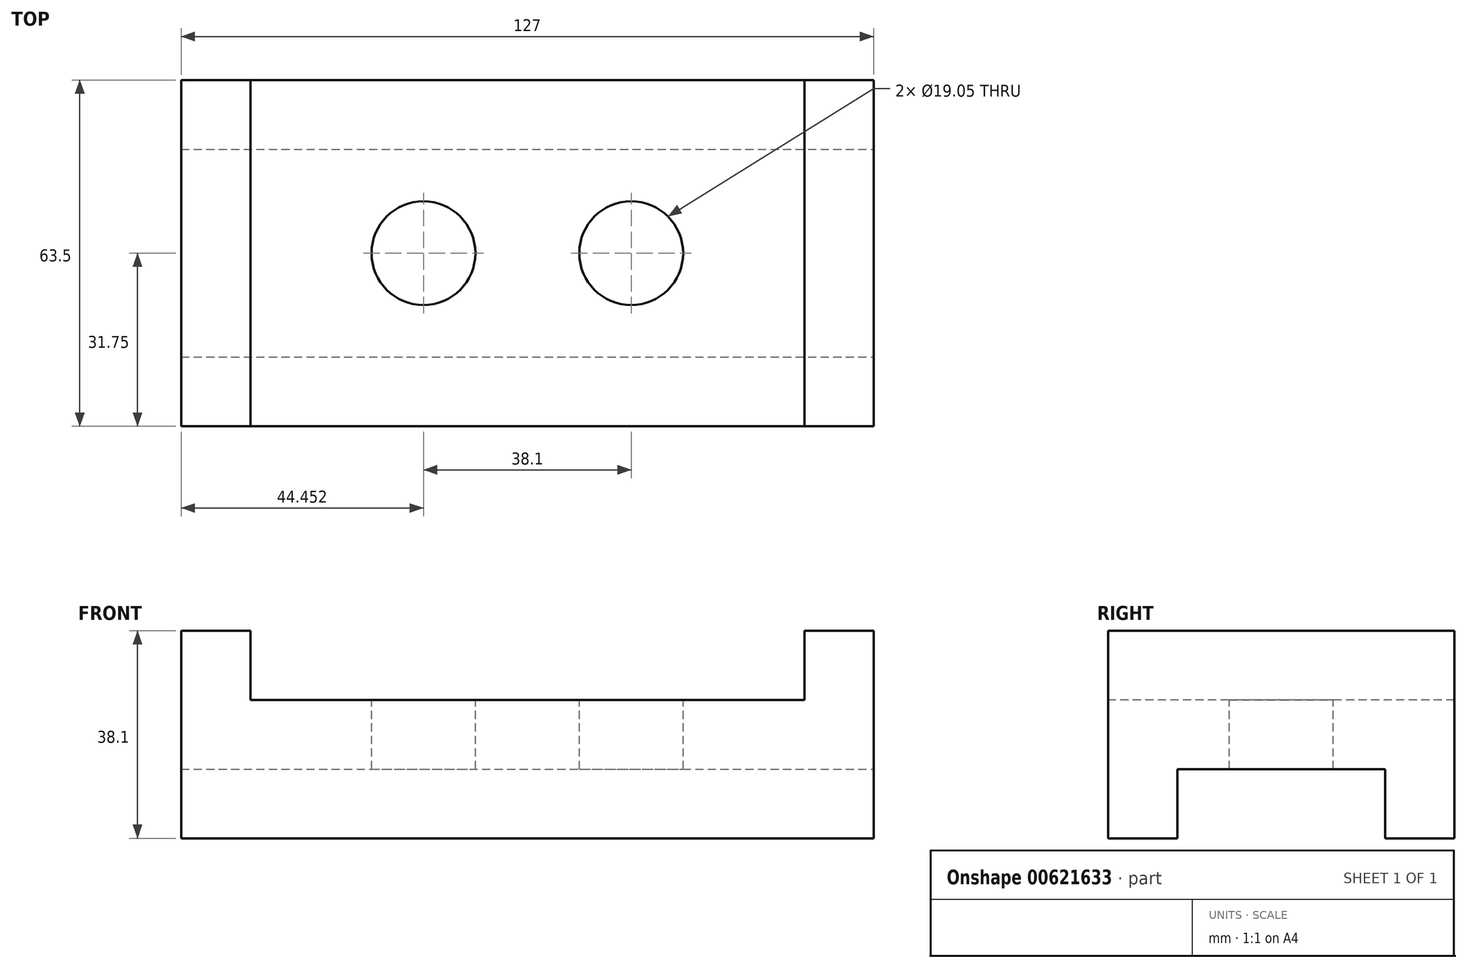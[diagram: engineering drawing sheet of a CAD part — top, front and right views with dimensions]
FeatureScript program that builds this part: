
annotation { "Feature Type Name" : "Feature", "Feature Type Description" : "" }
export const myFeature = defineFeature(function(context is Context, id is Id, definition is map)
    precondition{}
    {
        {
            var Q0;
            Q0=qCreatedBy(makeId("Front.planeOp"),FACE);
            var sketch = newSketch(context, id + "F0", { "sketchPlane" : qUnion([Q0])});
            skLineSegment(sketch, "E0.bottom", {"start": v(-60.49, 9.4) * mm, "end": v(66.51, 9.4) * mm});
            skLineSegment(sketch, "E0.top", {"start": v(-60.49, -28.7) * mm, "end": v(66.51, -28.7) * mm});
            skLineSegment(sketch, "E0.left", {"start": v(-60.49, 9.4) * mm, "end": v(-60.49, -28.7) * mm});
            skLineSegment(sketch, "E0.right", {"start": v(66.51, 9.4) * mm, "end": v(66.51, -28.7) * mm});
            skSolve(sketch);
        }
        {
            var Q0;
            Q0 = qSketchRegion(id + "F0", true);
            extrude(context, id + "F1", {"entities" : qUnion([Q0]), "depth" : 63.5 * mm, "offsetDistance" : 25.4 * mm});
        }
        {
            var Q0;
            Q0=makeQuery(id+"F1.opExtrude","CAP_FACE",FACE,{"disambiguationData":[OSD([sQuery(id+"F0.wireOp",EDGE,"E0.bottom"),sQuery(id+"F0.wireOp",EDGE,"E0.top"),sQuery(id+"F0.wireOp",EDGE,"E0.left"),sQuery(id+"F0.wireOp",EDGE,"E0.right")])],"isStart":false});
            var sketch = newSketch(context, id + "F2", { "sketchPlane" : qUnion([Q0])});
            skLineSegment(sketch, "E1.bottom", {"start": v(-47.79, 9.4) * mm, "end": v(53.81, 9.4) * mm});
            skLineSegment(sketch, "E1.top", {"start": v(-47.79, -3.3) * mm, "end": v(53.81, -3.3) * mm});
            skLineSegment(sketch, "E1.left", {"start": v(-47.79, 9.4) * mm, "end": v(-47.79, -3.3) * mm});
            skLineSegment(sketch, "E1.right", {"start": v(53.81, 9.4) * mm, "end": v(53.81, -3.3) * mm});
            skSolve(sketch);
        }
        {
            var Q0;
            Q0=makeQuery(id+"F2.imprint","IMPRINT",FACE,{"disambiguationData":[TD([[makeQuery(id+"F2.imprint","IMPRINT",EDGE,{"derivedFrom":sQuery(id+"F2.wireOp",EDGE,"E1.bottom")}),-1.0]])]});
            extrude(context, id + "F3", {"entities" : qUnion([Q0]), "operationType" : NewBodyOperationType.REMOVE, "endBound" : BoundingType.THROUGH_ALL, "oppositeDirection" : true, "depth" : 25.4 * mm, "offsetDistance" : 25.4 * mm});
        }
        {
            var Q0;
            Q0=makeQuery(id+"F1.opExtrude","SWEPT_FACE",FACE,{"disambiguationData":[OSD([sQuery(id+"F0.wireOp",EDGE,"E0.right")])]});
            var sketch = newSketch(context, id + "F4", { "sketchPlane" : qUnion([Q0])});
            skLineSegment(sketch, "E2.bottom", {"start": v(-50.8, -28.7) * mm, "end": v(-12.7, -28.7) * mm});
            skLineSegment(sketch, "E2.top", {"start": v(-50.8, -16) * mm, "end": v(-12.7, -16) * mm});
            skLineSegment(sketch, "E2.left", {"start": v(-50.8, -28.7) * mm, "end": v(-50.8, -16) * mm});
            skLineSegment(sketch, "E2.right", {"start": v(-12.7, -28.7) * mm, "end": v(-12.7, -16) * mm});
            skSolve(sketch);
        }
        {
            var Q0;
            Q0=makeQuery(id+"F4.imprint","IMPRINT",FACE,{"disambiguationData":[TD([[makeQuery(id+"F4.imprint","IMPRINT",EDGE,{"derivedFrom":sQuery(id+"F4.wireOp",EDGE,"E2.bottom")}),1.0]])]});
            extrude(context, id + "F5", {"entities" : qUnion([Q0]), "operationType" : NewBodyOperationType.REMOVE, "endBound" : BoundingType.THROUGH_ALL, "oppositeDirection" : true, "depth" : 25.4 * mm, "offsetDistance" : 25.4 * mm});
        }
        {
            var Q0;
            Q0=makeQuery(id+"F3.boolean.opBoolean","COPY",FACE,{"derivedFrom":makeQuery(id+"F3.opExtrude","SWEPT_FACE",FACE,{"disambiguationData":[OSD([sQuery(id+"F2.wireOp",EDGE,"E1.top")])]})});
            var sketch = newSketch(context, id + "F6", { "sketchPlane" : qUnion([Q0])});
            skCircle(sketch, "E3", {"center": v(-16.04, -31.75) * mm, "radius": 9.53 * mm});
            skPoint(sketch, "E3.centerSnap0", {"position": v(-47.79, -31.75) * mm});
            skCircle(sketch, "E4", {"center": v(22.06, -31.75) * mm, "radius": 9.53 * mm});
            skPoint(sketch, "E4.centerSnap0", {"position": v(53.81, -31.75) * mm});
            skSolve(sketch);
        }
        {
            var Q0;
            Q0=makeQuery(id+"F6.imprint","IMPRINT",FACE,{"disambiguationData":[TD([[makeQuery(id+"F6.imprint","IMPRINT",EDGE,{"derivedFrom":sQuery(id+"F6.wireOp",EDGE,"E3")}),1.0]])]});
            var Q1;
            Q1=makeQuery(id+"F6.imprint","IMPRINT",FACE,{"disambiguationData":[TD([[makeQuery(id+"F6.imprint","IMPRINT",EDGE,{"derivedFrom":sQuery(id+"F6.wireOp",EDGE,"E4")}),1.0]])]});
            extrude(context, id + "F7", {"entities" : qUnion([Q0, Q1]), "operationType" : NewBodyOperationType.REMOVE, "endBound" : BoundingType.THROUGH_ALL, "oppositeDirection" : true, "depth" : 25.4 * mm, "offsetDistance" : 25.4 * mm});
        }
    });
